FCSTD DOCUMENT  (FreeCAD 1.0R39319 (Git))
Label: ASSEMBLY-PO16-FRONTPANEL
License: All rights reserved
LicenseURL: https://en.wikipedia.org/wiki/All_rights_reserved
objects: App::Link×6, App::DocumentObjectGroup×3, PartDesign::CoordinateSystem×2, Part::FeaturePython×2, App::FeaturePython×1, App::Part×1
note: 4 computed .brp shape members not serialized (recipe doc carries the construction recipe); baked Part::Feature solids carry a one-line shape summary decoded from their .brp
EXTERNAL_REF file=Frontpanels/FRONTPANEL-VSN1-L.FCStd obj=LCS_1
EXTERNAL_REF file=Frontpanels/FRONTPANEL-XX16.FCStd obj=FP_XX16_3D_1
EXTERNAL_REF file=../Design/SCREW-M1.6x16/SCREW-M1.6x16.FCStd obj=LCS_1
EXTERNAL_REF file=Frontpanels/FRONTPANEL-XX16.FCStd obj=CircleAxis_1
EXTERNAL_REF file=../Design/SCREW-M1.6x16/SCREW-M1.6x16.FCStd obj=Body
EXTERNAL_REF file=Frontpanels/FRONTPANEL-XX16.FCStd obj=CircleAxis_2
EXTERNAL_REF file=Frontpanels/FRONTPANEL-XX16.FCStd obj=CircleAxis_3
EXTERNAL_REF file=Frontpanels/FRONTPANEL-XX16.FCStd obj=CircleAxis_4
EXTERNAL_REF file=../Design/PLASTIC-LIGHTPIPE/PLASTIC-LIGHTPIPE.FCStd obj=LCS_1
EXTERNAL_REF file=Frontpanels/FRONTPANEL-XX16.FCStd obj=CircleAxis_5
EXTERNAL_REF file=../Design/PLASTIC-LIGHTPIPE/PLASTIC-LIGHTPIPE.FCStd obj=Body

FEATURE [App::DocumentObjectGroup] Parts
FEATURE [PartDesign::CoordinateSystem] LCS_Origin
  AttacherType = Attacher::AttachEngine3D
  AttachmentSupport = -> [X_Axis]
  MapMode = 2
FEATURE [App::DocumentObjectGroup] Constraints
FEATURE [App::FeaturePython] Variables  # WARN: FeaturePython — macro-defined, semantics opaque (R4)
  Type = App::PropertyContainer
FEATURE [App::DocumentObjectGroup] Configurations
FEATURE [App::Link] FP_VSN1_L_3D_1  label="FP-VSN1-L-3D 1"
  AttachedBy = #LCS_1
  AttachedTo = Parent Assembly#LCS_Origin
  LinkedObject = -> <external Frontpanels/FRONTPANEL-XX16.FCStd>#FP_XX16_3D_1
  SolverId = Asm4EE
  expr: Placement = LCS_Origin.Placement * AttachmentOffset * FRONTPANEL_VSN1_L#LCS_1.Placement ^ -1
FEATURE [App::Link] SCREW_M1_6x16  label="SCREW-M1.6x16"
  AttachedBy = #LCS_1
  AttachedTo = FP_VSN1_L_3D_1#CircleAxis_1
  LinkPlacement = pos=(-50,50,0.91) rot=(0,0,1;0rad)
  LinkedObject = -> <external ../Design/SCREW-M1.6x16/SCREW-M1.6x16.FCStd>#Body
  Placement = pos=(-50,50,0.91) rot=(0,0,1;0rad)
  SolverId = Asm4EE
  expr: Placement = FP_VSN1_L_3D_1.Placement * Unnamed1#CircleAxis_1.Placement * AttachmentOffset * SCREW_M1_6x16#LCS_1.Placement ^ -1
FEATURE [App::Link] SCREW_M1_6x017  label="SCREW-M1.6x017"
  AttachedBy = #LCS_1
  AttachedTo = FP_VSN1_L_3D_1#CircleAxis_2
  LinkPlacement = pos=(50,50,0.91) rot=(0,0,1;0rad)
  LinkedObject = -> <external ../Design/SCREW-M1.6x16/SCREW-M1.6x16.FCStd>#Body
  Placement = pos=(50,50,0.91) rot=(0,0,1;0rad)
  SolverId = Asm4EE
  expr: Placement = FP_VSN1_L_3D_1.Placement * Unnamed1#CircleAxis_2.Placement * AttachmentOffset * SCREW_M1_6x16#LCS_1.Placement ^ -1
FEATURE [App::Link] SCREW_M1_6x018  label="SCREW-M1.6x018"
  AttachedBy = #LCS_1
  AttachedTo = FP_VSN1_L_3D_1#CircleAxis_3
  LinkPlacement = pos=(50,-50,0.91) rot=(0,0,1;0rad)
  LinkedObject = -> <external ../Design/SCREW-M1.6x16/SCREW-M1.6x16.FCStd>#Body
  Placement = pos=(50,-50,0.91) rot=(0,0,1;0rad)
  SolverId = Asm4EE
  expr: Placement = FP_VSN1_L_3D_1.Placement * Unnamed1#CircleAxis_3.Placement * AttachmentOffset * SCREW_M1_6x16#LCS_1.Placement ^ -1
FEATURE [App::Link] SCREW_M1_6x019  label="SCREW-M1.6x019"
  AttachedBy = #LCS_1
  AttachedTo = FP_VSN1_L_3D_1#CircleAxis_4
  LinkPlacement = pos=(-50,-50,0.91) rot=(0,0,1;0rad)
  LinkedObject = -> <external ../Design/SCREW-M1.6x16/SCREW-M1.6x16.FCStd>#Body
  Placement = pos=(-50,-50,0.91) rot=(0,0,1;0rad)
  SolverId = Asm4EE
  expr: Placement = FP_VSN1_L_3D_1.Placement * Unnamed1#CircleAxis_4.Placement * AttachmentOffset * SCREW_M1_6x16#LCS_1.Placement ^ -1
FEATURE [App::Link] PLASTIC_LIGHTPIPE  label="PLASTIC-LIGHTPIPE"
  AttachedBy = #LCS_1
  AttachedTo = FP_VSN1_L_3D_1#CircleAxis_5
  AttachmentOffset = pos=(0,0,0) rot=(1,0,0;3.14159rad)
  LinkPlacement = pos=(-40.005,48.505,0.91) rot=(0,0,-1;1.5708rad)
  LinkedObject = -> <external ../Design/PLASTIC-LIGHTPIPE/PLASTIC-LIGHTPIPE.FCStd>#Body
  Placement = pos=(-40.005,48.505,0.91) rot=(0,0,-1;1.5708rad)
  SolverId = Asm4EE
  expr: Placement = FP_VSN1_L_3D_1.Placement * Unnamed1#CircleAxis_5.Placement * AttachmentOffset * PLASTIC_LIGHTPIPE#LCS_1.Placement ^ -1
FEATURE [PartDesign::CoordinateSystem] LCS_1
  AttacherType = Attacher::AttachEngine3D
FEATURE [Part::FeaturePython] Linear_PLASTIC_LIGHTPIPE  label="Linear_PLASTIC-LIGHTPIPE"  # Draft array (typed FeaturePython)
  ArrayType = Linear Array
  Axis = -> LCS_1 [X]
  AxisPlacement = pos=(0,0,0) rot=(0.57735,0.57735,0.57735;2.0944rad)
  Count = 4
  Index = 1
  LinearStep = 26.67
  PlacementList = 4 placements: arithmetic series from (-40.005,48.505,0.91) step (26.67,0,2.9976e-15) to (40.005,48.505,0.91)
  Placer = pos=(0,0,80.01) rot=(0,0,1;0rad)
  ScaleList = (4) [(1,1,1),(1,1,1),(1,1,1),(1,1,1)]
  Scaler = 1
  ShowElement = false
  SourceObject = -> PLASTIC_LIGHTPIPE
  expr: .Placer.Base.z = LinearStep * Index
FEATURE [Part::FeaturePython] Linear_Linear_PLASTIC_LIGHTPIPE  label="Linear_Linear_PLASTIC-LIGHTPIPE"  # Draft array (typed FeaturePython)
  ArrayType = Linear Array
  Axis = -> LCS_1 [Y]
  AxisPlacement = pos=(0,0,0) rot=(0.57735,0.57735,0.57735;4.18879rad)
  Count = 4
  Index = 1
  LinearStep = -26.67
  PlacementList = 4 placements: arithmetic series from (0,0,0) step (-8.88289e-15,-26.67,8.88289e-15) to (-2.66487e-14,-80.01,2.66487e-14)
  Placer = pos=(0,0,-80.01) rot=(0,0,1;0rad)
  ScaleList = (4) [(1,1,1),(1,1,1),(1,1,1),(1,1,1)]
  Scaler = 1
  ShowElement = false
  SourceObject = -> Linear_PLASTIC_LIGHTPIPE
  expr: .Placer.Base.z = LinearStep * Index
FEATURE [App::Part] Assembly
  AssemblyType = Part::Link
  Group = -> [LCS_Origin,Constraints,Variables,Configurations,FP_VSN1_L_3D_1,SCREW_M1_6x16,SCREW_M1_6x017,SCREW_M1_6x018,SCREW_M1_6x019,PLASTIC_LIGHTPIPE,LCS_1,Linear_PLASTIC_LIGHTPIPE,Linear_Linear_PLASTIC_LIGHTPIPE]
  Origin = -> Origin
  Type = Assembly

RESOLVED EXTERNAL PARTS (link-assembly join: the EXTERNAL_REF files above that resolve inside this repo's crawl, each included once):
---- part ../Design/PLASTIC-LIGHTPIPE/PLASTIC-LIGHTPIPE.FCStd = doc fcstd_201000c635dd ----
FCSTD DOCUMENT  (FreeCAD 1.0R39319 (Git))
Label: PLASTIC-LIGHTPIPE
License: All rights reserved
LicenseURL: http://en.wikipedia.org/wiki/All_rights_reserved
objects: Sketcher::SketchObject×1, PartDesign::Revolution×1, PartDesign::CoordinateSystem×1, PartDesign::Body×1
note: 7 computed .brp shape members not serialized (recipe doc carries the construction recipe); baked Part::Feature solids carry a one-line shape summary decoded from their .brp

FEATURE [Sketcher::SketchObject] Sketch
  ArcFitTolerance = 0
  AttachmentSupport = -> [XZ_Plane]
  FullyConstrained = true
  MakeInternals = false
  MapMode = 5
  Placement = pos=(0,0,0) rot=(1,0,0;1.5708rad)
  expr: Constraints[4] = 2.8 / 2
  sketch-geometry (6):
    g0: LineSegment StartX=-1.4 StartY=0 StartZ=0 EndX=-1.4 EndY=-8 EndZ=0
    g1: LineSegment StartX=-1.4 StartY=-8 StartZ=0 EndX=0 EndY=-8 EndZ=0
    g2: LineSegment StartX=-1.65 StartY=0 StartZ=0 EndX=-1.65 EndY=0.2 EndZ=0
    g3: ArcOfCircle CenterX=0 CenterY=-2.30549 CenterZ=0 NormalX=0 NormalY=0 NormalZ=1 AngleXU=0 Radius=3 StartAngle=1.5708 EndAngle=2.15316
    g4: LineSegment StartX=2e-16 StartY=0.694506 StartZ=0 EndX=0 EndY=-8 EndZ=0
    g5: LineSegment StartX=-1.65 StartY=0 StartZ=0 EndX=-1.4 EndY=0 EndZ=0
  constraints (20):
    c: Vertical(g0)
    c: Coincident(g0,g1)
    c: PointOnObject(g1,g-2)
    c: Horizontal(g1)
    c: DistanceX(g1,g1) = 1.4
    c: Vertical(g2)
    c: PointOnObject(g3,g-2)
    c: PointOnObject(g3,g-2)
    c: Coincident(g3,g2)
    c: DistanceX(g2,g-1) = 1.65
    c: Radius(g3) = 3
    c: Coincident(g4,g3)
    c: Coincident(g4,g1)
    c: Coincident(g5,g2)
    c: Coincident(g5,g0)
    c: Horizontal(g5)
    c: DistanceY(g2,g2) = 0.2
    c: PointOnObject(g0,g-1)
    c: DistanceY(g0,g0) = 8
    c: DistanceY(g2,g3) = 0.694506
FEATURE [PartDesign::Revolution] Revolution
  Angle = 360
  Angle2 = 60
  Axis = (0,2e-16,1)
  Base = (0,0,0)
  Placement = pos=(0,0,0) rot=(1,0,0;1.5708rad)
  Profile = -> Sketch
  ReferenceAxis = -> Sketch [V_Axis]
  Suppressed = false
  Type = 0
FEATURE [PartDesign::CoordinateSystem] LCS_1
  AttacherType = Attacher::AttachEngine3D
FEATURE [PartDesign::Body] Body  label="PLASTIC-LIGHTPIPE"
  AllowCompound = false
  Group = -> [Sketch,Revolution,LCS_1]
  Origin = -> Origin
  Tip = -> Revolution
---- part ../Design/SCREW-M1.6x16/SCREW-M1.6x16.FCStd = doc fcstd_4ed8d198f377 ----
FCSTD DOCUMENT  (FreeCAD 1.0R39319 (Git))
Label: SCREW-M1.6x16
License: All rights reserved
LicenseURL: https://en.wikipedia.org/wiki/All_rights_reserved
objects: Sketcher::SketchObject×3, PartDesign::Revolution×1, PartDesign::Pocket×1, PartDesign::Fillet×1, PartDesign::AdditiveHelix×1, PartDesign::CoordinateSystem×1, PartDesign::Body×1
note: 20 computed .brp shape members not serialized (recipe doc carries the construction recipe); baked Part::Feature solids carry a one-line shape summary decoded from their .brp

FEATURE [Sketcher::SketchObject] Sketch  label="Profile"
  ArcFitTolerance = 0
  AttachmentSupport = -> [XZ_Plane]
  FullyConstrained = true
  MakeInternals = false
  MapMode = 5
  Placement = pos=(0,0,0) rot=(1,0,0;1.5708rad)
  sketch-geometry (6):
    g0: LineSegment StartX=1e-16 StartY=1.3 StartZ=0 EndX=0 EndY=-16 EndZ=0
    g1: LineSegment StartX=-1.6 StartY=0 StartZ=0 EndX=-0.6105 EndY=0 EndZ=0
    g2: LineSegment StartX=-0.6105 StartY=0 StartZ=0 EndX=-0.6105 EndY=-16 EndZ=0
    g3: LineSegment StartX=0 StartY=-16 StartZ=0 EndX=-0.6105 EndY=-16 EndZ=0
    g4: LineSegment StartX=-1.6 StartY=0 StartZ=0 EndX=-1.6 EndY=0.5 EndZ=0
    g5: ArcOfCircle CenterX=0 CenterY=-0.7 CenterZ=0 NormalX=0 NormalY=0 NormalZ=1 AngleXU=0 Radius=2 StartAngle=1.5708 EndAngle=2.49809
  constraints (19):
    c: PointOnObject(g0,g-2)
    c: Horizontal(g1)
    c: Coincident(g2,g1)
    c: Vertical(g2)
    c: Coincident(g3,g0)
    c: Horizontal(g3)
    c: Coincident(g2,g3)
    c: DistanceX(g3,g3) = 0.6105
    c: Distance(g2) = 16  'L'
    c: DistanceY(g1,g0) = 1.3
    c: Distance(g1,g0) = 1.6
    c: Coincident(g4,g1)
    c: Vertical(g4)
    c: PointOnObject(g5,g0)
    c: Coincident(g5,g0)
    c: Coincident(g5,g4)
    c: DistanceY(g4,g4) = 0.5
    c: PointOnObject(g0,g-2)
    c: PointOnObject(g1,g-1)
FEATURE [PartDesign::Revolution] Revolution
  Angle = 360
  Angle2 = 60
  Axis = (0,2e-16,1)
  Base = (0,0,0)
  Placement = pos=(0,0,0) rot=(1,0,0;1.5708rad)
  Profile = -> Sketch
  ReferenceAxis = -> Sketch [V_Axis]
  Suppressed = false
  Type = 0
FEATURE [Sketcher::SketchObject] Sketch001
  ArcFitTolerance = 0
  AttachmentSupport = -> [XZ_Plane]
  ExternalGeometry = -> [Revolution]
  FullyConstrained = true
  MakeInternals = false
  MapMode = 5
  Placement = pos=(0,0,0) rot=(1,0,0;1.5708rad)
  sketch-geometry (9):
    g0: LineSegment StartX=-0.6105 StartY=-16 StartZ=0 EndX=-0.7905 EndY=-15.8961 EndZ=0
    g1: LineSegment StartX=-0.7905 StartY=-15.8961 StartZ=0 EndX=-0.6105 EndY=-15.7922 EndZ=0
    g2: LineSegment [constr] StartX=-0.6105 StartY=-15.7922 StartZ=0 EndX=0 EndY=-15.7922 EndZ=0
    g3: LineSegment [constr] StartX=0 StartY=-15.7922 StartZ=0 EndX=0 EndY=-16 EndZ=0
    g4: LineSegment [constr] StartX=-0.6105 StartY=-16 StartZ=0 EndX=0 EndY=-16 EndZ=0
    g5: LineSegment [constr] StartX=-0.6105 StartY=-15.7922 StartZ=0 EndX=-0.6105 EndY=-16 EndZ=0
    g6: LineSegment StartX=-0.6105 StartY=-15.7922 StartZ=0 EndX=-0.5605 EndY=-15.7922 EndZ=0
    g7: LineSegment StartX=-0.5605 StartY=-15.7922 StartZ=0 EndX=-0.5605 EndY=-16 EndZ=0
    g8: LineSegment StartX=-0.5605 StartY=-16 StartZ=0 EndX=-0.6105 EndY=-16 EndZ=0
  constraints (23):
    c: Angle(g0,g1) = 1.0472
    c: Equal(g1,g0)
    c: Coincident(g0,g1)
    c: Coincident(g2,g1)
    c: Horizontal(g2)
    c: Coincident(g3,g2)
    c: Coincident(g0,g-3)
    c: Vertical(g1,g0)
    c: Vertical(g3)
    c: DistanceX(g0,g2) = 0.7905
    c: Symmetric(g0,g-3,g3)
    c: Coincident(g4,g0)
    c: Coincident(g4,g3)
    c: Coincident(g5,g1)
    c: Coincident(g5,g0)
    c: Coincident(g6,g1)
    c: PointOnObject(g6,g2)
    c: Coincident(g7,g6)
    c: PointOnObject(g7,g4)
    c: Vertical(g7)
    c: Coincident(g8,g7)
    c: Coincident(g8,g0)
    c: DistanceX(g6,g6) = 0.05
FEATURE [Sketcher::SketchObject] Sketch002
  ArcFitTolerance = 0
  FullyConstrained = true
  MakeInternals = false
  MapMode = 5
  Placement = pos=(-1e-16,2.1e-15,0.5) rot=(0.707107,0.707107,0;3.14159rad)
  sketch-geometry (14):
    g0: LineSegment StartX=-0.25 StartY=-0.8 StartZ=0 EndX=-0.25 EndY=-0.25 EndZ=0
    g1: LineSegment StartX=-0.25 StartY=0.8 StartZ=0 EndX=0.25 EndY=0.8 EndZ=0
    g2: LineSegment StartX=0.25 StartY=0.8 StartZ=0 EndX=0.25 EndY=0.25 EndZ=0
    g3: LineSegment StartX=0.25 StartY=-0.8 StartZ=0 EndX=-0.25 EndY=-0.8 EndZ=0
    g4: GeomPoint [constr] X=0 Y=0 Z=0
    g5: LineSegment StartX=-0.8 StartY=0.25 StartZ=0 EndX=-0.8 EndY=-0.25 EndZ=0
    g6: LineSegment StartX=-0.8 StartY=-0.25 StartZ=0 EndX=-0.25 EndY=-0.25 EndZ=0
    g7: LineSegment StartX=0.8 StartY=-0.25 StartZ=0 EndX=0.8 EndY=0.25 EndZ=0
    g8: LineSegment StartX=0.8 StartY=0.25 StartZ=0 EndX=0.25 EndY=0.25 EndZ=0
    g9: GeomPoint [constr] X=0 Y=0 Z=0
    g10: LineSegment StartX=-0.25 StartY=0.25 StartZ=0 EndX=-0.25 EndY=0.8 EndZ=0
    g11: LineSegment StartX=0.25 StartY=-0.25 StartZ=0 EndX=0.8 EndY=-0.25 EndZ=0
    g12: LineSegment StartX=-0.25 StartY=0.25 StartZ=0 EndX=-0.8 EndY=0.25 EndZ=0
    g13: LineSegment StartX=0.25 StartY=-0.25 StartZ=0 EndX=0.25 EndY=-0.8 EndZ=0
  constraints (36):
    c: Coincident(g10,g1)
    c: Coincident(g1,g2)
    c: Coincident(g13,g3)
    c: Coincident(g3,g0)
    c: Horizontal(g1)
    c: Horizontal(g3)
    c: Vertical(g0)
    c: Vertical(g2)
    c: Symmetric(g1,g0,g4)
    c: Coincident(g4,g-1)
    c: Coincident(g5,g6)
    c: Coincident(g11,g7)
    c: Coincident(g7,g8)
    c: Coincident(g12,g5)
    c: Horizontal(g6)
    c: Horizontal(g8)
    c: Vertical(g5)
    c: Vertical(g7)
    c: Symmetric(g11,g5,g9)
    c: Coincident(g9,g4)
    c: Distance(g1) = 0.5
    c: Distance(g7) = 0.5
    c: Coincident(g6,g0)
    c: Vertical(g10)
    c: Vertical(g10,g0)
    c: Coincident(g12,g10)
    c: Coincident(g2,g8)
    c: Coincident(g13,g11)
    c: Horizontal(g12)
    c: DistanceX(g5,g7) = 1.6
    c: Vertical(g13)
    c: DistanceY(g3,g1) = 1.6
    c: Horizontal(g11)
    c: Horizontal(g2,g10)
    c: Horizontal(g11,g0)
    c: Vertical(g2,g11)
FEATURE [PartDesign::Pocket] Pocket
  BaseFeature = -> Revolution
  Direction = (-1e-16,1e-16,1)
  Length = 1
  Length2 = 5
  Placement = pos=(0,0,0) rot=(1,0,0;1.5708rad)
  Profile = -> Sketch002
  ReferenceAxis = -> Sketch002 [N_Axis]
  Refine = true
  Suppressed = false
  Type = 1
FEATURE [PartDesign::Fillet] Fillet
  Base = -> Pocket [Edge43,Edge37,Edge25,Edge31]
  BaseFeature = -> Pocket
  Placement = pos=(0,0,0) rot=(1,0,0;1.5708rad)
  Radius = 0.1
  Refine = true
  SupportTransform = false
  Suppressed = false
  UseAllEdges = false
FEATURE [PartDesign::AdditiveHelix] AdditiveHelix
  Angle = 0
  Axis = (0,2e-16,1)
  Base = (0,0,0)
  BaseFeature = -> Fillet
  Growth = 0
  HasBeenEdited = true
  Height = 16
  LeftHanded = false
  Mode = 0
  Outside = false
  Pitch = 0.35
  Placement = pos=(0,0,0) rot=(1,0,0;1.5708rad)
  Profile = -> Sketch001
  ReferenceAxis = -> Sketch001 [V_Axis]
  Suppressed = false
  Tolerance = 0.1
  Turns = 45.7143
  expr: Height = <<Profile>>.Constraints.L
FEATURE [PartDesign::CoordinateSystem] LCS_1
  AttacherType = Attacher::AttachEngine3D
FEATURE [PartDesign::Body] Body  label="SCREW-M1.6x16"
  AllowCompound = false
  Group = -> [Sketch,Revolution,Pocket,Fillet,Sketch001,AdditiveHelix,Sketch002,LCS_1]
  Origin = -> Origin
  Tip = -> AdditiveHelix
---- part Frontpanels/FRONTPANEL-VSN1-L.FCStd = doc fcstd_41c90e056a76 ----
FCSTD DOCUMENT  (FreeCAD 1.0R39319 (Git))
Label: FRONTPANEL-VSN1-L
License: All rights reserved
LicenseURL: https://en.wikipedia.org/wiki/All_rights_reserved
objects: PartDesign::Line×9, Part::Feature×1, PartDesign::CoordinateSystem×1, App::Part×1, PartDesign::FeatureBase×1, Sketcher::SketchObject×1, PartDesign::Pocket×1, PartDesign::Body×1
note: 19 computed .brp shape members not serialized (recipe doc carries the construction recipe); baked Part::Feature solids carry a one-line shape summary decoded from their .brp

FEATURE [Part::Feature] Part__Feature  label="kibot_u2ziuiw0_PCB"
  shape: bbox 105.6 x 105.6 x 0.91 mm, 180 faces (baked)
FEATURE [PartDesign::CoordinateSystem] LCS_1
  AttacherType = Attacher::AttachEngine3D
  MapMode = 1
FEATURE [PartDesign::Line] CircleAxis_1
  AttacherType = Attacher::AttachEngineLine
  AttachmentSupport = -> [Part__Feature]
  Length = 8.17259
  MapMode = 19
  Placement = pos=(5.82492,36.3902,0.91) rot=(0.707107,-0.707107,0;3.14159rad)
  ResizeMode = 1
FEATURE [PartDesign::Line] CircleAxis_2
  AttacherType = Attacher::AttachEngineLine
  AttachmentSupport = -> [Part__Feature]
  Length = 8.17259
  MapMode = 19
  Placement = pos=(7.8295,39.8623,0.91) rot=(0.707107,-0.707107,0;3.14159rad)
  ResizeMode = 1
FEATURE [PartDesign::Line] CircleAxis_3
  AttacherType = Attacher::AttachEngineLine
  AttachmentSupport = -> [Part__Feature]
  Length = 8.17259
  MapMode = 19
  Placement = pos=(10.4065,42.9335,0.91) rot=(0.707107,-0.707107,0;3.14159rad)
  ResizeMode = 1
FEATURE [PartDesign::Line] CircleAxis_4
  AttacherType = Attacher::AttachEngineLine
  AttachmentSupport = -> [Part__Feature]
  Length = 8.17259
  MapMode = 19
  Placement = pos=(13.4777,45.5105,0.91) rot=(0.707107,-0.707107,0;3.14159rad)
  ResizeMode = 1
FEATURE [PartDesign::Line] CircleAxis_5
  AttacherType = Attacher::AttachEngineLine
  AttachmentSupport = -> [Part__Feature]
  Length = 8.17259
  MapMode = 19
  Placement = pos=(16.9498,47.5151,0.91) rot=(0.707107,-0.707107,0;3.14159rad)
  ResizeMode = 1
FEATURE [PartDesign::Line] CircleAxis_6
  AttacherType = Attacher::AttachEngineLine
  AttachmentSupport = -> [Part__Feature]
  Length = 4.93174
  MapMode = 19
  Placement = pos=(-50,50,0.91) rot=(0,0,1;0rad)
  ResizeMode = 1
FEATURE [PartDesign::Line] CircleAxis_7
  AttacherType = Attacher::AttachEngineLine
  AttachmentSupport = -> [Part__Feature]
  Length = 4.93174
  MapMode = 19
  Placement = pos=(50,50,0.91) rot=(0,0,1;0rad)
  ResizeMode = 1
FEATURE [PartDesign::Line] CircleAxis_8
  AttacherType = Attacher::AttachEngineLine
  AttachmentSupport = -> [Part__Feature]
  Length = 4.93174
  MapMode = 19
  Placement = pos=(50,-50,0.91) rot=(0,0,1;0rad)
  ResizeMode = 1
FEATURE [PartDesign::Line] CircleAxis_9
  AttacherType = Attacher::AttachEngineLine
  AttachmentSupport = -> [Part__Feature]
  Length = 4.93174
  MapMode = 19
  Placement = pos=(-50,-50,0.91) rot=(0,0,1;0rad)
  ResizeMode = 1
FEATURE [App::Part] FP_VSN1_L_3D_1  label="FP-VSN1-L-3D 1"
  Group = -> [Part__Feature,LCS_1,CircleAxis_1,CircleAxis_2,CircleAxis_3,CircleAxis_4,CircleAxis_5,CircleAxis_6,CircleAxis_7,CircleAxis_8,CircleAxis_9]
  Origin = -> Origin
FEATURE [PartDesign::FeatureBase] Clone
  BaseFeature = -> Part__Feature
  Suppressed = false
FEATURE [Sketcher::SketchObject] Sketch
  ArcFitTolerance = 1e-06
  AttachmentSupport = -> [XY_Plane002]
  FullyConstrained = true
  MakeInternals = false
  MapMode = 5
  sketch-geometry (13):
    g0: LineSegment StartX=-46.92 StartY=9.22 StartZ=0 EndX=-6.42 EndY=9.22 EndZ=0
    g1: LineSegment StartX=-4.12 StartY=11.52 StartZ=0 EndX=-4.12 EndY=41.82 EndZ=0
    g2: LineSegment StartX=-6.42 StartY=44.12 StartZ=0 EndX=-46.92 EndY=44.12 EndZ=0
    g3: LineSegment StartX=-49.22 StartY=41.82 StartZ=0 EndX=-49.22 EndY=11.52 EndZ=0
    g4: GeomPoint [constr] X=-26.67 Y=26.67 Z=0
    g5: ArcOfCircle CenterX=-46.92 CenterY=41.82 CenterZ=0 NormalX=0 NormalY=0 NormalZ=1 AngleXU=0 Radius=2.3 StartAngle=1.5708 EndAngle=3.14159
    g6: GeomPoint [constr] X=-49.22 Y=44.12 Z=0
    g7: ArcOfCircle CenterX=-46.92 CenterY=11.52 CenterZ=0 NormalX=0 NormalY=0 NormalZ=1 AngleXU=0 Radius=2.3 StartAngle=3.14159 EndAngle=4.71239
    g8: GeomPoint [constr] X=-49.22 Y=9.22 Z=0
    g9: ArcOfCircle CenterX=-6.42 CenterY=11.52 CenterZ=0 NormalX=0 NormalY=0 NormalZ=1 AngleXU=0 Radius=2.3 StartAngle=4.71239 EndAngle=6.28319
    g10: GeomPoint [constr] X=-4.12 Y=9.22 Z=0
    g11: ArcOfCircle CenterX=-6.42 CenterY=41.82 CenterZ=0 NormalX=0 NormalY=0 NormalZ=1 AngleXU=0 Radius=2.3 StartAngle=1.1e-15 EndAngle=1.5708
    g12: GeomPoint [constr] X=-4.12 Y=44.12 Z=0
  constraints (29):
    c: Horizontal(g0)
    c: Horizontal(g2)
    c: Vertical(g1)
    c: Vertical(g3)
    c: Symmetric(g12,g8,g4)
    c: PointOnObject(g6,g2)
    c: PointOnObject(g6,g3)
    c: Tangent(g2,g5) = -1.5708
    c: Tangent(g3,g5) = -1.5708
    c: PointOnObject(g8,g3)
    c: PointOnObject(g8,g0)
    c: Tangent(g3,g7) = -1.5708
    c: Tangent(g0,g7) = -1.5708
    c: PointOnObject(g10,g0)
    c: PointOnObject(g10,g1)
    c: Tangent(g0,g9) = -1.5708
    c: Tangent(g1,g9) = -1.5708
    c: PointOnObject(g12,g1)
    c: PointOnObject(g12,g2)
    c: Tangent(g1,g11) = -1.5708
    c: Tangent(g2,g11) = -1.5708
    c: Distance(g1,g3) = 45.1
    c: Distance(g2,g0) = 34.9
    c: Equal(g5,g11)
    c: Equal(g9,g7)
    c: Equal(g7,g5)
    c: Radius(g5) = 2.3
    c: Distance(g4,g-1) = 26.67
    c: Distance(g4,g-2) = 26.67
FEATURE [PartDesign::Pocket] Pocket
  BaseFeature = -> Clone
  Direction = (0,0,-1)
  Length = 5
  Length2 = 5
  Midplane = true
  Profile = -> Sketch
  ReferenceAxis = -> Sketch [N_Axis]
  Refine = true
  Suppressed = false
  Type = 1
FEATURE [PartDesign::Body] Body001
  AllowCompound = false
  Group = -> [Clone,Sketch,Pocket]
  Origin = -> Origin002
  Tip = -> Pocket
